# Revit family: Faucet-Handle-KOHLER-Core-K-EX36796T
name_source: partatom
category: Specialty Equipment
units: mm (PartAtom-declared; Revit-internal decimal feet)

## family parameters
Cut with Voids When Loaded = No
Host = Face
OmniClass Number = 23.31.25.00
Part Type = Normal
Room Calculation Point = No
Round Connector Dimension = Use Diameter
Shared = No

## types (3) — shared parameters
ADA Compliant = No
Assembly Code = C1030200
Date Modified = 09/03/2024
Default Elevation = 42"
Description = Handle
Handle Clearance = 2 5/8"
Height = 1 1/16"
Length = 2 5/8"
Manufacturer = Kohler Co.
Master Format 2014 = 10 28 00
Master Format 2014 Name = Toilet, Bath, and Laundry Accessories
Material = Plastic
Product Name = Core
WaterSense Certified = No
Width = 2 5/8"

## per-type parameters (varying)
| type | Finish | Model | Plug Finish | Type | URL |
| 2BP-Blue | Kohler-Plastic-2BP-Blue | K-EX36796T-9-2BP | Silicone-Pantone-423C | 1 | https://www.us.kohler.com |
| BPT-Black | Kohler-Plastic-BPT-Black | K-EX36796T-9-BPT | Plastic-Pantone-Black_C | 2 | https://www.us.kohler.com |
| WPL-White | Kohler-Plastic-WPL-White | K-EX36796T-9-WPL | Silicone-Pantone-423C | 3 | http://www.kohler.com.cn |

## geometry (parser evidence)
native form markers: Sweep x5
no freeform markers — native parametric forms only
